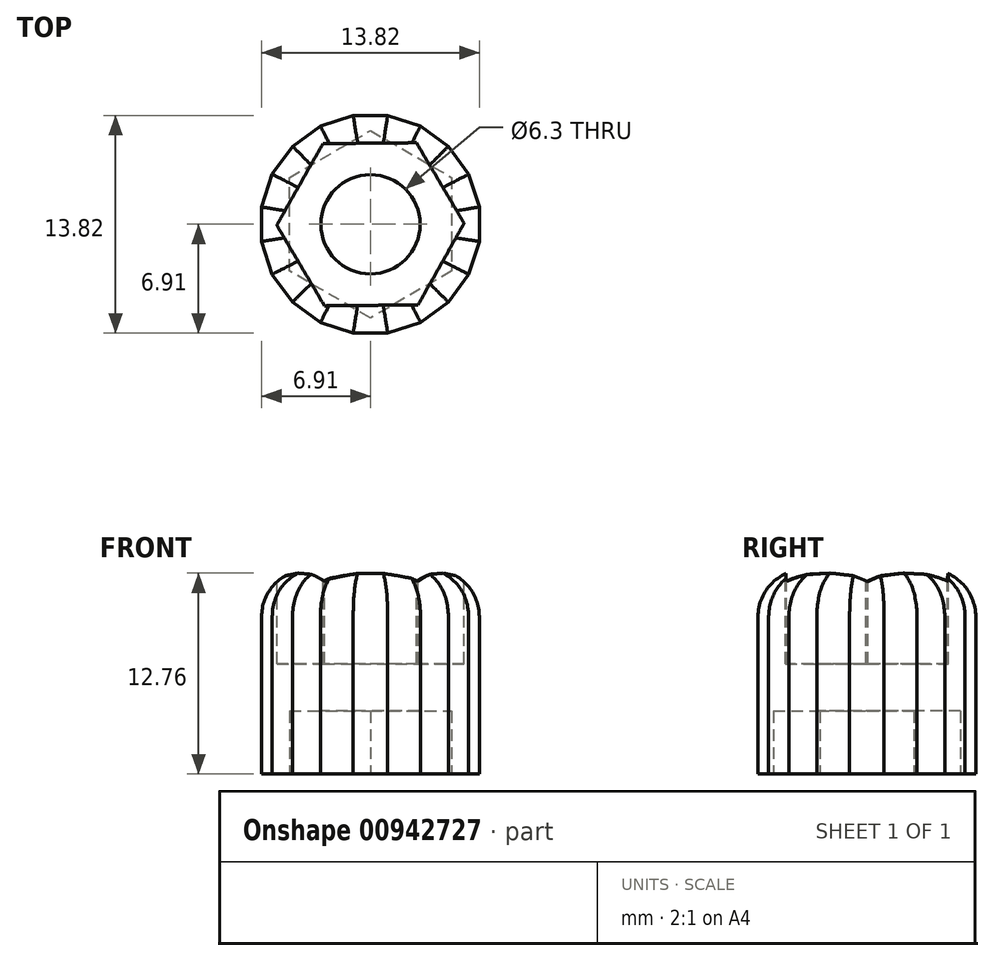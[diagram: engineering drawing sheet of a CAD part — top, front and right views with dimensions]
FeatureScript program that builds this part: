
annotation { "Feature Type Name" : "Feature", "Feature Type Description" : "" }
export const myFeature = defineFeature(function(context is Context, id is Id, definition is map)
    precondition{}
    {
        {
            var Q0;
            Q0=qCreatedBy(makeId("Top.planeOp"),FACE);
            var sketch = newSketch(context, id + "F0", { "sketchPlane" : qUnion([Q0])});
            skCircle(sketch, "E0.cCircle", {"center": v(0, 0) * mm, "radius": 6.91 * mm, "construction": true});
            skLineSegment(sketch, "E0.0", {"start": v(6.91, 1.1) * mm, "end": v(6.91, -1.1) * mm});
            skLineSegment(sketch, "E0.1", {"start": v(6.91, -1.1) * mm, "end": v(6.24, -3.18) * mm});
            skLineSegment(sketch, "E0.2", {"start": v(6.24, -3.18) * mm, "end": v(4.95, -4.95) * mm});
            skLineSegment(sketch, "E0.3", {"start": v(4.95, -4.95) * mm, "end": v(3.18, -6.24) * mm});
            skLineSegment(sketch, "E0.4", {"start": v(3.18, -6.24) * mm, "end": v(1.1, -6.91) * mm});
            skLineSegment(sketch, "E0.5", {"start": v(1.1, -6.91) * mm, "end": v(-1.1, -6.91) * mm});
            skLineSegment(sketch, "E0.6", {"start": v(-1.1, -6.91) * mm, "end": v(-3.18, -6.24) * mm});
            skLineSegment(sketch, "E0.7", {"start": v(-3.18, -6.24) * mm, "end": v(-4.95, -4.95) * mm});
            skLineSegment(sketch, "E0.8", {"start": v(-4.95, -4.95) * mm, "end": v(-6.24, -3.18) * mm});
            skLineSegment(sketch, "E0.9", {"start": v(-6.24, -3.18) * mm, "end": v(-6.91, -1.1) * mm});
            skLineSegment(sketch, "E0.10", {"start": v(-6.91, -1.1) * mm, "end": v(-6.91, 1.1) * mm});
            skLineSegment(sketch, "E0.11", {"start": v(-6.91, 1.1) * mm, "end": v(-6.24, 3.18) * mm});
            skLineSegment(sketch, "E0.12", {"start": v(-6.24, 3.18) * mm, "end": v(-4.95, 4.95) * mm});
            skLineSegment(sketch, "E0.13", {"start": v(-4.95, 4.95) * mm, "end": v(-3.18, 6.24) * mm});
            skLineSegment(sketch, "E0.14", {"start": v(-3.18, 6.24) * mm, "end": v(-1.1, 6.91) * mm});
            skLineSegment(sketch, "E0.15", {"start": v(-1.1, 6.91) * mm, "end": v(1.1, 6.91) * mm});
            skLineSegment(sketch, "E0.16", {"start": v(1.1, 6.91) * mm, "end": v(3.18, 6.24) * mm});
            skLineSegment(sketch, "E0.17", {"start": v(3.18, 6.24) * mm, "end": v(4.95, 4.95) * mm});
            skLineSegment(sketch, "E0.18", {"start": v(4.95, 4.95) * mm, "end": v(6.24, 3.18) * mm});
            skLineSegment(sketch, "E0.19", {"start": v(6.24, 3.18) * mm, "end": v(6.91, 1.1) * mm});
            skPoint(sketch, "E0.0.midPoint", {"position": v(6.91, 0) * mm});
            skCircle(sketch, "E1.cCircle", {"center": v(0, 0) * mm, "radius": 5.15 * mm, "construction": true});
            skLineSegment(sketch, "E1.0", {"start": v(5.15, 2.97) * mm, "end": v(5.15, -2.97) * mm});
            skLineSegment(sketch, "E1.1", {"start": v(5.15, -2.97) * mm, "end": v(0, -5.95) * mm});
            skLineSegment(sketch, "E1.2", {"start": v(0, -5.95) * mm, "end": v(-5.15, -2.97) * mm});
            skLineSegment(sketch, "E1.3", {"start": v(-5.15, -2.97) * mm, "end": v(-5.15, 2.97) * mm});
            skLineSegment(sketch, "E1.4", {"start": v(-5.15, 2.97) * mm, "end": v(0, 5.95) * mm});
            skLineSegment(sketch, "E1.5", {"start": v(0, 5.95) * mm, "end": v(5.15, 2.97) * mm});
            skPoint(sketch, "E1.0.midPoint", {"position": v(5.15, 0) * mm});
            skCircle(sketch, "E2", {"center": v(0, 0) * mm, "radius": 3.15 * mm});
            skSolve(sketch);
        }
        {
            var Q0;
            Q0=makeQuery(id+"F0.imprint","IMPRINT",FACE,{"disambiguationData":[TD([[makeQuery(id+"F0.imprint","IMPRINT",EDGE,{"derivedFrom":sQuery(id+"F0.wireOp",EDGE,"E0.0")}),-1.0]])]});
            var Q1;
            Q1=makeQuery(id+"F0.imprint","IMPRINT",FACE,{"disambiguationData":[TD([[makeQuery(id+"F0.imprint","IMPRINT",EDGE,{"derivedFrom":sQuery(id+"F0.wireOp",EDGE,"E1.0")}),-1.0]])]});
            extrude(context, id + "F1", {"entities" : qUnion([Q0, Q1]), "depth" : 13 * mm, "offsetDistance" : 25 * mm});
        }
        {
            var Q0;
            Q0=makeQuery(id+"F0.imprint","IMPRINT",FACE,{"disambiguationData":[TD([[makeQuery(id+"F0.imprint","IMPRINT",EDGE,{"derivedFrom":sQuery(id+"F0.wireOp",EDGE,"E1.0")}),-1.0]])]});
            extrude(context, id + "F2", {"entities" : qUnion([Q0]), "operationType" : NewBodyOperationType.REMOVE, "flatOperationType" : FlatOperationType.REMOVE, "depth" : 4 * mm, "offsetDistance" : 25 * mm, "domain" : OperationDomain.MODEL});
        }
        {
            var Q0;
            Q0=makeQuery(id+"F1.opExtrude","CAP_FACE",FACE,{"disambiguationData":[OSD([sQuery(id+"F0.wireOp",EDGE,"E0.0"),sQuery(id+"F0.wireOp",EDGE,"E0.1"),sQuery(id+"F0.wireOp",EDGE,"E0.2"),sQuery(id+"F0.wireOp",EDGE,"E0.3"),sQuery(id+"F0.wireOp",EDGE,"E0.4"),sQuery(id+"F0.wireOp",EDGE,"E0.5"),sQuery(id+"F0.wireOp",EDGE,"E0.6"),sQuery(id+"F0.wireOp",EDGE,"E0.7"),sQuery(id+"F0.wireOp",EDGE,"E0.8"),sQuery(id+"F0.wireOp",EDGE,"E0.9"),sQuery(id+"F0.wireOp",EDGE,"E0.10"),sQuery(id+"F0.wireOp",EDGE,"E0.11"),sQuery(id+"F0.wireOp",EDGE,"E0.12"),sQuery(id+"F0.wireOp",EDGE,"E0.13"),sQuery(id+"F0.wireOp",EDGE,"E0.14"),sQuery(id+"F0.wireOp",EDGE,"E0.15"),sQuery(id+"F0.wireOp",EDGE,"E0.16"),sQuery(id+"F0.wireOp",EDGE,"E0.17"),sQuery(id+"F0.wireOp",EDGE,"E0.18"),sQuery(id+"F0.wireOp",EDGE,"E0.19"),sQuery(id+"F0.wireOp",EDGE,"E2")])],"isStart":false});
            var sketch = newSketch(context, id + "F3", { "sketchPlane" : qUnion([Q0])});
            skCircle(sketch, "E3.cCircle", {"center": v(0, 0) * mm, "radius": 5.15 * mm, "construction": true});
            skLineSegment(sketch, "E3.0", {"start": v(-5.95, -0.06) * mm, "end": v(-3.02, 5.12) * mm});
            skLineSegment(sketch, "E3.1", {"start": v(-3.02, 5.12) * mm, "end": v(2.92, 5.18) * mm});
            skLineSegment(sketch, "E3.2", {"start": v(2.92, 5.18) * mm, "end": v(5.95, 0.06) * mm});
            skLineSegment(sketch, "E3.3", {"start": v(5.95, 0.06) * mm, "end": v(3.02, -5.12) * mm});
            skLineSegment(sketch, "E3.4", {"start": v(3.02, -5.12) * mm, "end": v(-2.92, -5.18) * mm});
            skLineSegment(sketch, "E3.5", {"start": v(-2.92, -5.18) * mm, "end": v(-5.95, -0.06) * mm});
            skPoint(sketch, "E3.0.midPoint", {"position": v(-4.48, 2.53) * mm});
            skSolve(sketch);
        }
        {
            var Q0;
            Q0=makeQuery(id+"F3.imprint","IMPRINT",FACE,{"disambiguationData":[TD([[makeQuery(id+"F3.imprint","IMPRINT",EDGE,{"derivedFrom":sQuery(id+"F3.wireOp",EDGE,"E3.0")}),-1.0]])]});
            extrude(context, id + "F4", {"entities" : qUnion([Q0]), "operationType" : NewBodyOperationType.REMOVE, "oppositeDirection" : true, "depth" : 6 * mm, "offsetDistance" : 25 * mm});
        }
        {
            var Q0;
            Q0=makeQuery(id+"F1.opExtrude","CAP_EDGE",EDGE,{"disambiguationData":[OSD([sQuery(id+"F0.wireOp",EDGE,"E0.1")])],"isStart":false});
            var Q1;
            Q1=makeQuery(id+"F1.opExtrude","CAP_EDGE",EDGE,{"disambiguationData":[OSD([sQuery(id+"F0.wireOp",EDGE,"E0.2")])],"isStart":false});
            var Q2;
            Q2=makeQuery(id+"F1.opExtrude","CAP_EDGE",EDGE,{"disambiguationData":[OSD([sQuery(id+"F0.wireOp",EDGE,"E0.3")])],"isStart":false});
            var Q3;
            Q3=makeQuery(id+"F1.opExtrude","CAP_EDGE",EDGE,{"disambiguationData":[OSD([sQuery(id+"F0.wireOp",EDGE,"E0.4")])],"isStart":false});
            var Q4;
            Q4=makeQuery(id+"F1.opExtrude","CAP_EDGE",EDGE,{"disambiguationData":[OSD([sQuery(id+"F0.wireOp",EDGE,"E0.5")])],"isStart":false});
            var Q5;
            Q5=makeQuery(id+"F1.opExtrude","CAP_EDGE",EDGE,{"disambiguationData":[OSD([sQuery(id+"F0.wireOp",EDGE,"E0.6")])],"isStart":false});
            var Q6;
            Q6=makeQuery(id+"F1.opExtrude","CAP_EDGE",EDGE,{"disambiguationData":[OSD([sQuery(id+"F0.wireOp",EDGE,"E0.7")])],"isStart":false});
            var Q7;
            Q7=makeQuery(id+"F1.opExtrude","CAP_EDGE",EDGE,{"disambiguationData":[OSD([sQuery(id+"F0.wireOp",EDGE,"E0.8")])],"isStart":false});
            var Q8;
            Q8=makeQuery(id+"F1.opExtrude","CAP_EDGE",EDGE,{"disambiguationData":[OSD([sQuery(id+"F0.wireOp",EDGE,"E0.9")])],"isStart":false});
            var Q9;
            Q9=makeQuery(id+"F1.opExtrude","CAP_EDGE",EDGE,{"disambiguationData":[OSD([sQuery(id+"F0.wireOp",EDGE,"E0.10")])],"isStart":false});
            var Q10;
            Q10=makeQuery(id+"F1.opExtrude","CAP_EDGE",EDGE,{"disambiguationData":[OSD([sQuery(id+"F0.wireOp",EDGE,"E0.11")])],"isStart":false});
            var Q11;
            Q11=makeQuery(id+"F1.opExtrude","CAP_EDGE",EDGE,{"disambiguationData":[OSD([sQuery(id+"F0.wireOp",EDGE,"E0.12")])],"isStart":false});
            var Q12;
            Q12=makeQuery(id+"F1.opExtrude","CAP_EDGE",EDGE,{"disambiguationData":[OSD([sQuery(id+"F0.wireOp",EDGE,"E0.13")])],"isStart":false});
            var Q13;
            Q13=makeQuery(id+"F1.opExtrude","CAP_EDGE",EDGE,{"disambiguationData":[OSD([sQuery(id+"F0.wireOp",EDGE,"E0.14")])],"isStart":false});
            var Q14;
            Q14=makeQuery(id+"F1.opExtrude","CAP_EDGE",EDGE,{"disambiguationData":[OSD([sQuery(id+"F0.wireOp",EDGE,"E0.15")])],"isStart":false});
            var Q15;
            Q15=makeQuery(id+"F1.opExtrude","CAP_EDGE",EDGE,{"disambiguationData":[OSD([sQuery(id+"F0.wireOp",EDGE,"E0.16")])],"isStart":false});
            var Q16;
            Q16=makeQuery(id+"F1.opExtrude","CAP_EDGE",EDGE,{"disambiguationData":[OSD([sQuery(id+"F0.wireOp",EDGE,"E0.17")])],"isStart":false});
            var Q17;
            Q17=makeQuery(id+"F1.opExtrude","CAP_EDGE",EDGE,{"disambiguationData":[OSD([sQuery(id+"F0.wireOp",EDGE,"E0.18")])],"isStart":false});
            var Q18;
            Q18=makeQuery(id+"F1.opExtrude","CAP_EDGE",EDGE,{"disambiguationData":[OSD([sQuery(id+"F0.wireOp",EDGE,"E0.19")])],"isStart":false});
            var Q19;
            Q19=makeQuery(id+"F1.opExtrude","CAP_EDGE",EDGE,{"disambiguationData":[OSD([sQuery(id+"F0.wireOp",EDGE,"E0.0")])],"isStart":false});
            fillet(context, id + "F5", {"entities" : qUnion([Q0, Q1, Q2, Q3, Q4, Q5, Q6, Q7, Q8, Q9, Q10, Q11, Q12, Q13, Q14, Q15, Q16, Q17, Q18, Q19]), "radius" : 3 * mm, "tangentPropagation" : true, "allowEdgeOverflow" : false});
        }
    });
